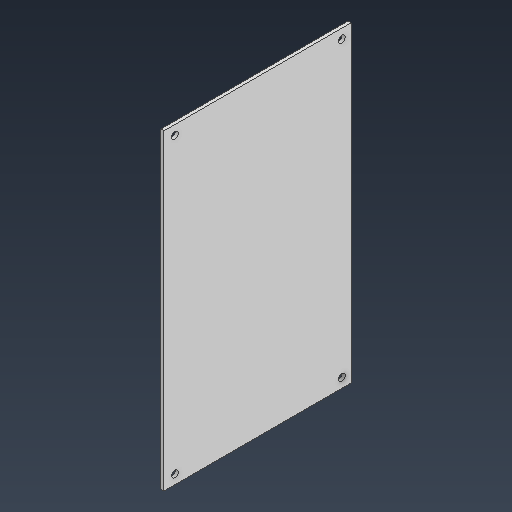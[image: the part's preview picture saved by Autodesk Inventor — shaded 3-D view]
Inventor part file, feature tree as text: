
AUTODESK INVENTOR PART (.ipt)
format: ipt  version: 2025.3 (Build 293356000, 356)  size: 91,136 bytes
history: native  units: mm
features: extrude x1, sketch x1
ambient origin geometry x8: Origin, YZ Plane, XZ Plane, XY Plane, X Axis, Y Axis, Z Axis, Center Point
bodies: Solid1 (feature_tree)
feature tree (2):
  extrude  "Extrusion1"  Depth=60.0mm
  sketch  "Sketch1"  dims[d0=100.0mm d1=60.0mm d2=2.2mm d3=2.2mm d4=3.5mm d5=3.0mm d6=3.0mm d7=3.0mm d8=3.0mm d9=1.0mm d10=0.0mm]
